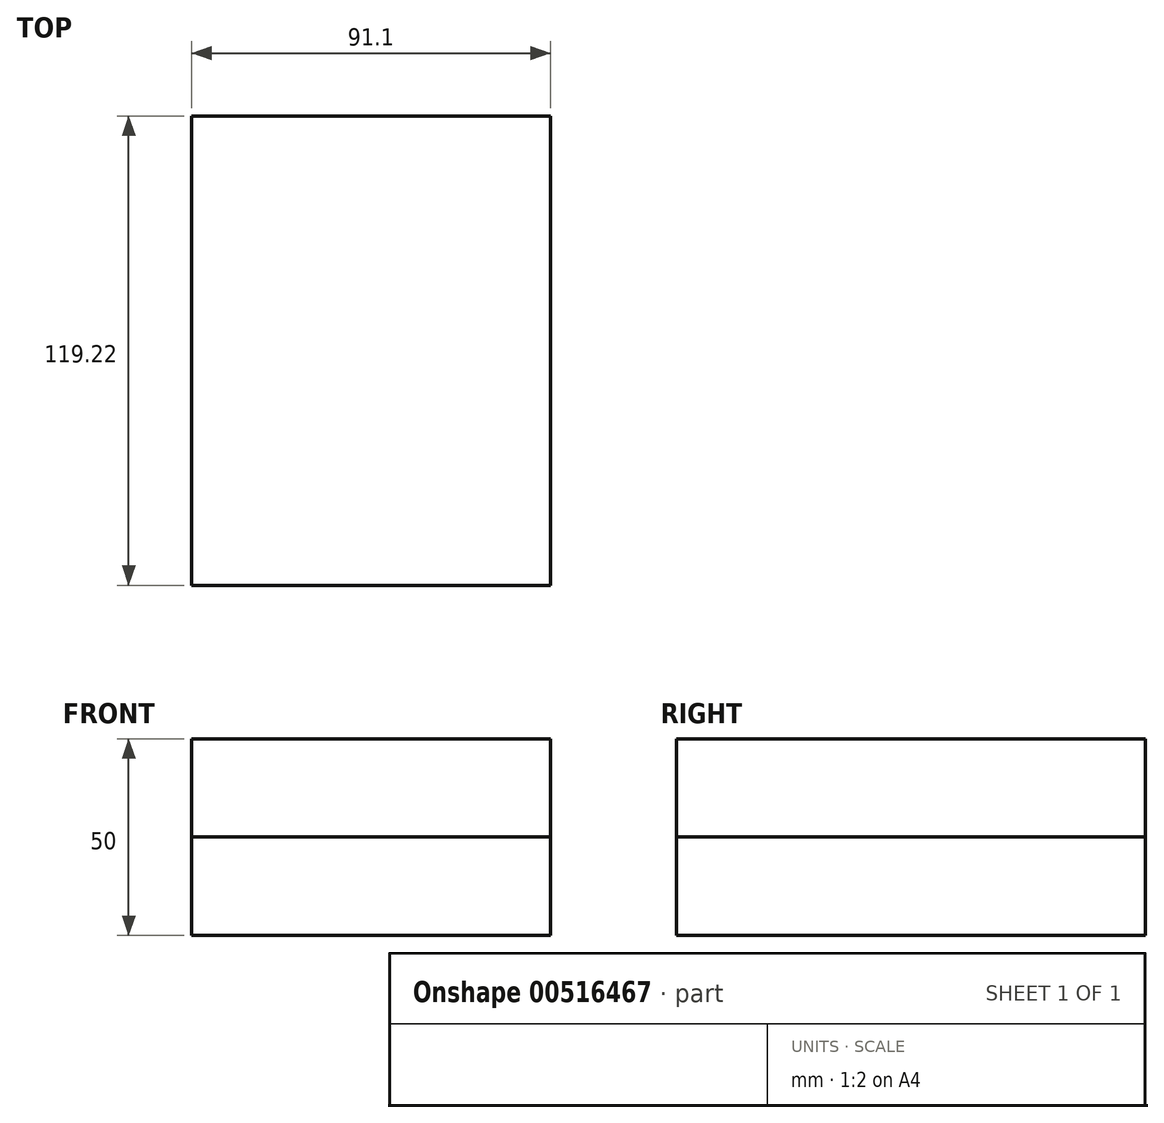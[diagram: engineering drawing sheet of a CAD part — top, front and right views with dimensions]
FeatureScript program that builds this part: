
annotation { "Feature Type Name" : "Feature", "Feature Type Description" : "" }
export const myFeature = defineFeature(function(context is Context, id is Id, definition is map)
    precondition{}
    {
        {
            var Q0;
            Q0=qCreatedBy(makeId("Top.planeOp"),FACE);
            var sketch = newSketch(context, id + "F0", { "sketchPlane" : qUnion([Q0])});
            skLineSegment(sketch, "E0.bottom", {"start": v(0, 0) * mm, "end": v(0, 0) * mm});
            skLineSegment(sketch, "E0.top", {"start": v(0, 0) * mm, "end": v(0, 0) * mm});
            skLineSegment(sketch, "E0.left", {"start": v(0, 0) * mm, "end": v(0, 0) * mm});
            skLineSegment(sketch, "E0.right", {"start": v(0, 0) * mm, "end": v(0, 0) * mm});
            skPoint(sketch, "E0.middle", {"position": v(0, 0) * mm});
            skLineSegment(sketch, "E1.bottom", {"start": v(45.55, -59.6) * mm, "end": v(-45.55, -59.6) * mm});
            skLineSegment(sketch, "E1.top", {"start": v(45.55, 59.6) * mm, "end": v(-45.55, 59.6) * mm});
            skLineSegment(sketch, "E1.left", {"start": v(45.55, -59.6) * mm, "end": v(45.55, 59.6) * mm});
            skLineSegment(sketch, "E1.right", {"start": v(-45.55, -59.6) * mm, "end": v(-45.55, 59.6) * mm});
            skSolve(sketch);
        }
        {
            var Q0;
            Q0=makeQuery(id+"F0.imprint","IMPRINT",FACE,{"disambiguationData":[TD([[makeQuery(id+"F0.imprint","IMPRINT",EDGE,{"derivedFrom":sQuery(id+"F0.wireOp",EDGE,"E1.bottom")}),-1.0]])]});
            extrude(context, id + "F1", {"entities" : qUnion([Q0]), "endBound" : BoundingType.SYMMETRIC, "depth" : 50 * mm, "offsetDistance" : 25 * mm});
        }
        {
            var Q0;
            Q0 = qSketchRegion(id + "F0", true);
            extrude(context, id + "F2", {"entities" : qUnion([Q0]), "depth" : 25 * mm, "offsetDistance" : 25 * mm});
        }
    });
